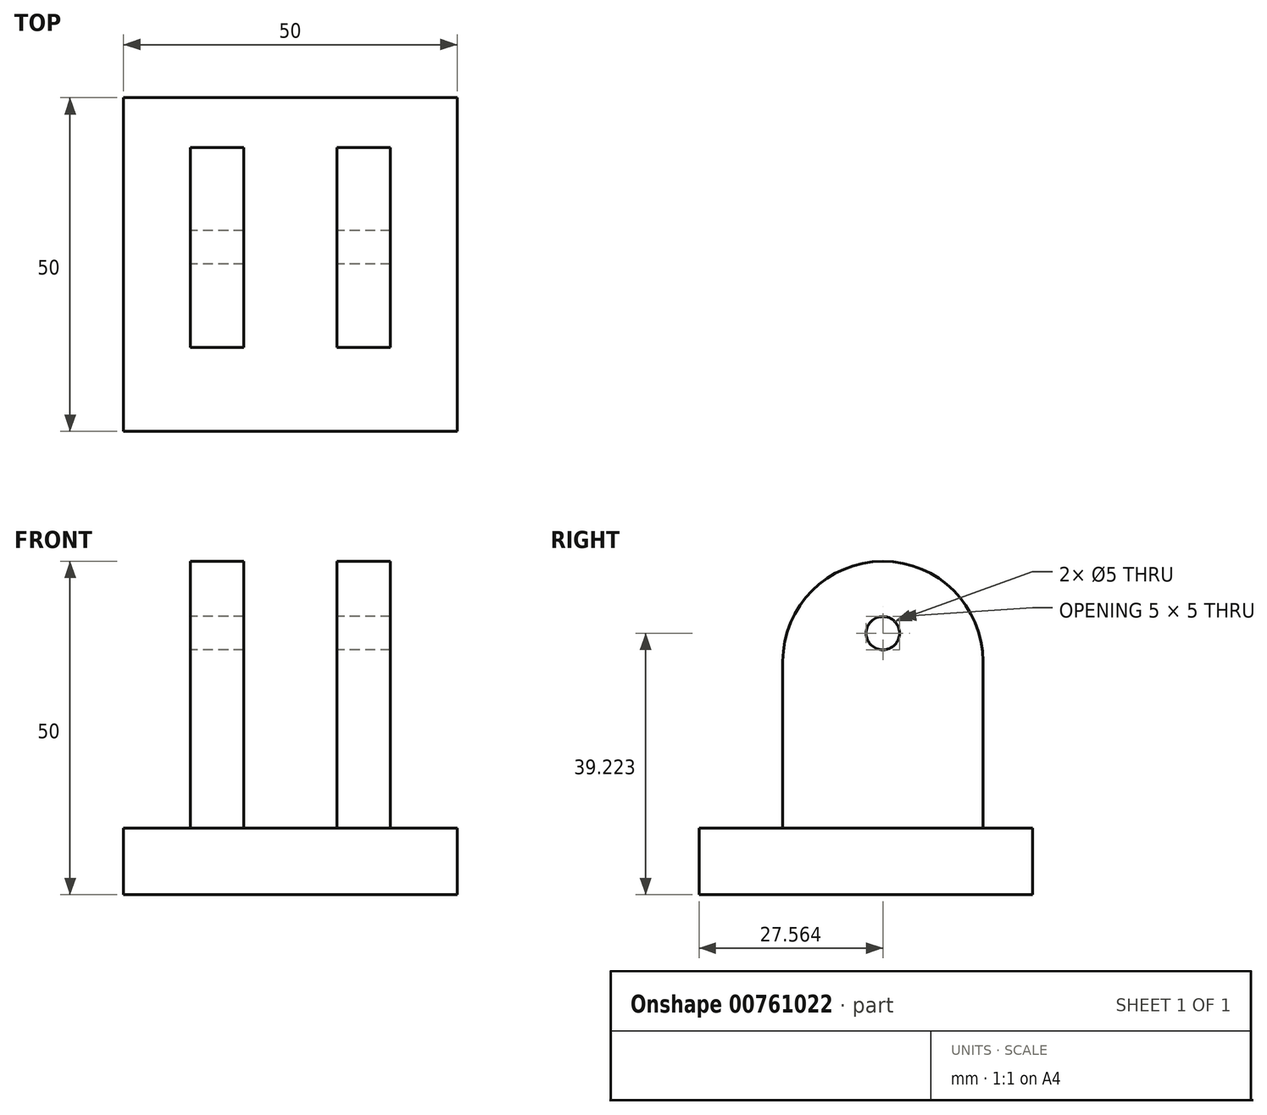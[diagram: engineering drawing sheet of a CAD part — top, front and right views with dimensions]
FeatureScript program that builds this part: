
annotation { "Feature Type Name" : "Feature", "Feature Type Description" : "" }
export const myFeature = defineFeature(function(context is Context, id is Id, definition is map)
    precondition{}
    {
        {
            var Q0;
            Q0=qCreatedBy(makeId("Top.planeOp"),FACE);
            var sketch = newSketch(context, id + "F0", { "sketchPlane" : qUnion([Q0])});
            skLineSegment(sketch, "E0.bottom", {"start": v(-22.36, 26.57) * mm, "end": v(27.64, 26.57) * mm});
            skLineSegment(sketch, "E0.top", {"start": v(-22.36, -23.43) * mm, "end": v(27.64, -23.43) * mm});
            skLineSegment(sketch, "E0.left", {"start": v(-22.36, 26.57) * mm, "end": v(-22.36, -23.43) * mm});
            skLineSegment(sketch, "E0.right", {"start": v(27.64, 26.57) * mm, "end": v(27.64, -23.43) * mm});
            skSolve(sketch);
        }
        {
            var Q0;
            Q0 = qSketchRegion(id + "F0", true);
            extrude(context, id + "F1", {"entities" : qUnion([Q0]), "depth" : 10 * mm, "offsetDistance" : 25 * mm});
        }
        {
            var Q0;
            Q0=makeQuery(id+"F1.opExtrude","CAP_FACE",FACE,{"disambiguationData":[OSD([sQuery(id+"F0.wireOp",EDGE,"E0.bottom"),sQuery(id+"F0.wireOp",EDGE,"E0.top"),sQuery(id+"F0.wireOp",EDGE,"E0.left"),sQuery(id+"F0.wireOp",EDGE,"E0.right")])],"isStart":false});
            var sketch = newSketch(context, id + "F2", { "sketchPlane" : qUnion([Q0])});
            skLineSegment(sketch, "E1.bottom", {"start": v(-12.36, 19.13) * mm, "end": v(-4.36, 19.13) * mm});
            skLineSegment(sketch, "E1.top", {"start": v(-12.36, -10.87) * mm, "end": v(-4.36, -10.87) * mm});
            skLineSegment(sketch, "E1.left", {"start": v(-12.36, 19.13) * mm, "end": v(-12.36, -10.87) * mm});
            skLineSegment(sketch, "E1.right", {"start": v(-4.36, 19.13) * mm, "end": v(-4.36, -10.87) * mm});
            skLineSegment(sketch, "E2.bottom", {"start": v(9.64, 19.13) * mm, "end": v(17.64, 19.13) * mm});
            skLineSegment(sketch, "E2.top", {"start": v(9.64, -10.87) * mm, "end": v(17.64, -10.87) * mm});
            skLineSegment(sketch, "E2.left", {"start": v(9.64, 19.13) * mm, "end": v(9.64, -10.87) * mm});
            skLineSegment(sketch, "E2.right", {"start": v(17.64, 19.13) * mm, "end": v(17.64, -10.87) * mm});
            skSolve(sketch);
        }
        {
            var Q0;
            Q0 = qSketchRegion(id + "F2", true);
            extrude(context, id + "F3", {"entities" : qUnion([Q0]), "operationType" : NewBodyOperationType.ADD, "depth" : 40 * mm, "offsetDistance" : 25 * mm});
        }
        {
            var Q0;
            Q0=makeQuery(id+"F3.opExtrude","CAP_EDGE",EDGE,{"disambiguationData":[OSD([sQuery(id+"F2.wireOp",EDGE,"E2.top")])],"isStart":false});
            var Q1;
            Q1=makeQuery(id+"F3.opExtrude","CAP_EDGE",EDGE,{"disambiguationData":[OSD([sQuery(id+"F2.wireOp",EDGE,"E2.bottom")])],"isStart":false});
            var Q2;
            Q2=makeQuery(id+"F3.opExtrude","CAP_EDGE",EDGE,{"disambiguationData":[OSD([sQuery(id+"F2.wireOp",EDGE,"E1.bottom")])],"isStart":false});
            var Q3;
            Q3=makeQuery(id+"F3.opExtrude","CAP_EDGE",EDGE,{"disambiguationData":[OSD([sQuery(id+"F2.wireOp",EDGE,"E1.top")])],"isStart":false});
            fillet(context, id + "F4", {"entities" : qUnion([Q0, Q1, Q2, Q3]), "radius" : 15 * mm, "tangentPropagation" : true, "allowEdgeOverflow" : false});
        }
        {
            var Q0;
            Q0=makeQuery(id+"F3.opExtrude","SWEPT_FACE",FACE,{"disambiguationData":[OSD([sQuery(id+"F2.wireOp",EDGE,"E1.left")])]});
            var sketch = newSketch(context, id + "F5", { "sketchPlane" : qUnion([Q0])});
            skCircle(sketch, "E3", {"center": v(-4.13, 39.22) * mm, "radius": 2.5 * mm});
            skPoint(sketch, "E3.centerSnap0", {"position": v(-4.13, 50) * mm});
            skSolve(sketch);
        }
        {
            var Q0;
            Q0=sQuery(id+"F5.wireOp",VERTEX,"E3.center");
            var Q1;
            Q1=makeQuery(id+"F1.opExtrude","SWEPT_BODY",BODY,{"disambiguationData":[OSD([sQuery(id+"F0.wireOp",EDGE,"E0.bottom"),sQuery(id+"F0.wireOp",EDGE,"E0.top"),sQuery(id+"F0.wireOp",EDGE,"E0.left"),sQuery(id+"F0.wireOp",EDGE,"E0.right")])]});
            hole(context, id + "F6", {"style" : HoleStyle.SIMPLE, "endStyle" : HoleEndStyle.THROUGH, "holeDiameter" : 5 * mm, "majorDiameter" : 5 * mm, "isTappedThrough" : true, "tappedDepth" : 12 * mm, "tapClearance" : 3, "locations" : qUnion([Q0]), "scope" : qUnion([Q1])});
        }
    });
